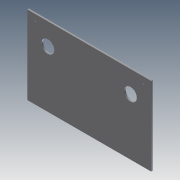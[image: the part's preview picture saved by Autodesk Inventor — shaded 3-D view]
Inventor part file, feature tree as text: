
AUTODESK INVENTOR PART (.ipt)
format: ipt  version: 2011 (Build 150239000, 239)  size: 424,448 bytes
history: native  units: in
note: dims shown in document units (in); Inventor stores cm internally (conversion verified against a paired STEP export)
features: extrude x21, sketch x21
ambient origin geometry x8: Origin, YZ Plane, XZ Plane, XY Plane, X Axis, Y Axis, Z Axis, Center Point
bodies: Solid1 (feature_tree)
feature tree (42):
  extrude  "Extrusion1"  Depth=12.85in
  extrude  "Extrusion2"  Depth=0.75in
  extrude  "Extrusion3"  Depth=2.0in
  extrude  "Extrusion4"  Depth=2.0in
  extrude  "Extrusion5"  Depth=2.0in
  extrude  "Extrusion6"  Depth=2.0in
  extrude  "Extrusion7"  Depth=2.0in
  extrude  "Extrusion8"  Depth=0.75in
  extrude  "Extrusion9"  Depth=0.25in TaperAngle=0.0deg
  extrude  "Extrusion10"  Depth=2.0in
  extrude  "Extrusion11"  Depth=7.175in
  extrude  "Extrusion12"  Depth=2.0in
  extrude  "Extrusion13"  Depth=2.0in
  extrude  "Extrusion14"  Depth=2.0in
  extrude  "Extrusion15"  Depth=0.25in TaperAngle=0.0deg
  extrude  "Extrusion16"  Depth=3.0in
  extrude  "Extrusion17"  Depth=3.0in
  extrude  "Extrusion18"  Depth=2.0in
  extrude  "Extrusion19"  Depth=1.0in TaperAngle=0.0deg
  extrude  "Extrusion20"  Depth=0.25in TaperAngle=0.0deg
  extrude  "Extrusion21"  Depth=0.25in TaperAngle=0.0deg
  sketch  "Sketch1"  dims[d0=19.5in d1=12.85in]
  sketch  "Sketch2"  dims[d2=0.25in d3=0.0in d4=0.75in]
  sketch  "Sketch3"  dims[d5=0.25in d6=2.0in]
  sketch  "Sketch4"  dims[d7=2.0in d8=2.0in]
  sketch  "Sketch5"  dims[d9=2.0in d10=2.0in]
  sketch  "Sketch6"  dims[d11=2.0in d12=2.0in]
  sketch  "Sketch7"  dims[d13=2.0in d14=2.0in]
  sketch  "Sketch8"  dims[d15=0.25in d16=0.0in d17=0.75in]
  sketch  "Sketch9"  dims[d18=0.25in d19=0.25in d20=0.0in]
  sketch  "Sketch10"  dims[d21=2.0in d22=2.0in]
  sketch  "Sketch12"  dims[d23=0.25in d24=0.0in d25=7.175in]
  sketch  "Sketch13"  dims[d26=0.25in d27=2.0in]
  sketch  "Sketch14"  dims[d28=2.0in d29=2.0in]
  sketch  "Sketch15"  dims[d30=2.0in d31=2.0in]
  sketch  "Sketch16"  dims[d32=0.25in d33=0.25in d34=0.0in]
  sketch  "Sketch17"  dims[d35=0.25in d36=0.0in d37=3.0in]
  sketch  "Sketch18"  dims[d38=3.0in d39=3.0in]
  sketch  "Sketch19"  dims[d40=3.0in d41=2.0in]
  sketch  "Sketch20"  dims[d42=2.0in d43=1.0in d44=0.0in]
  sketch  "Sketch21"  dims[d45=0.25in d46=0.0in d47=0.25in d48=0.0in]
  sketch  "Sketch22"  dims[d49=0.25in d50=0.0in d51=0.25in d52=0.0in d53=3.5in d54=3.25in d55=3.25in d56=2.0in d57=2.0in d58=0.25in d59=0.0in d60=0.25in d61=0.0in d62=3.25in d63=3.438in d64=3.25in d65=3.438in d66=2.0in d67=2.0in d68=0.25in d69=0.0in d70=1.25in d71=1.0in d72=2.25in d73=2.25in d74=1.25in d75=2.25in d76=0.156in d77=0.156in d78=0.156in d79=0.156in d80=1.0in d81=0.0in d82=10.35in d83=1.0in d84=1.0in d85=1.0in d86=0.156in d87=0.156in d88=1.0in d89=0.0in d90=0.25in d91=0.0in d92=10.35in d93=1.0in d94=1.0in d95=0.156in d96=0.25in d97=0.0in d98=0.315in d99=1.1811in d100=0.3937in d101=0.3937in d102=0.25in d103=0.0in d104=1.5in d105=1.0in d106=2.0in d107=1.0in d108=1.0in d109=0.75in d110=0.5in d111=0.75in d112=0.5in d113=0.25in d114=0.0in d115=10.105in d116=0.156in d117=0.25in d118=0.0in]
